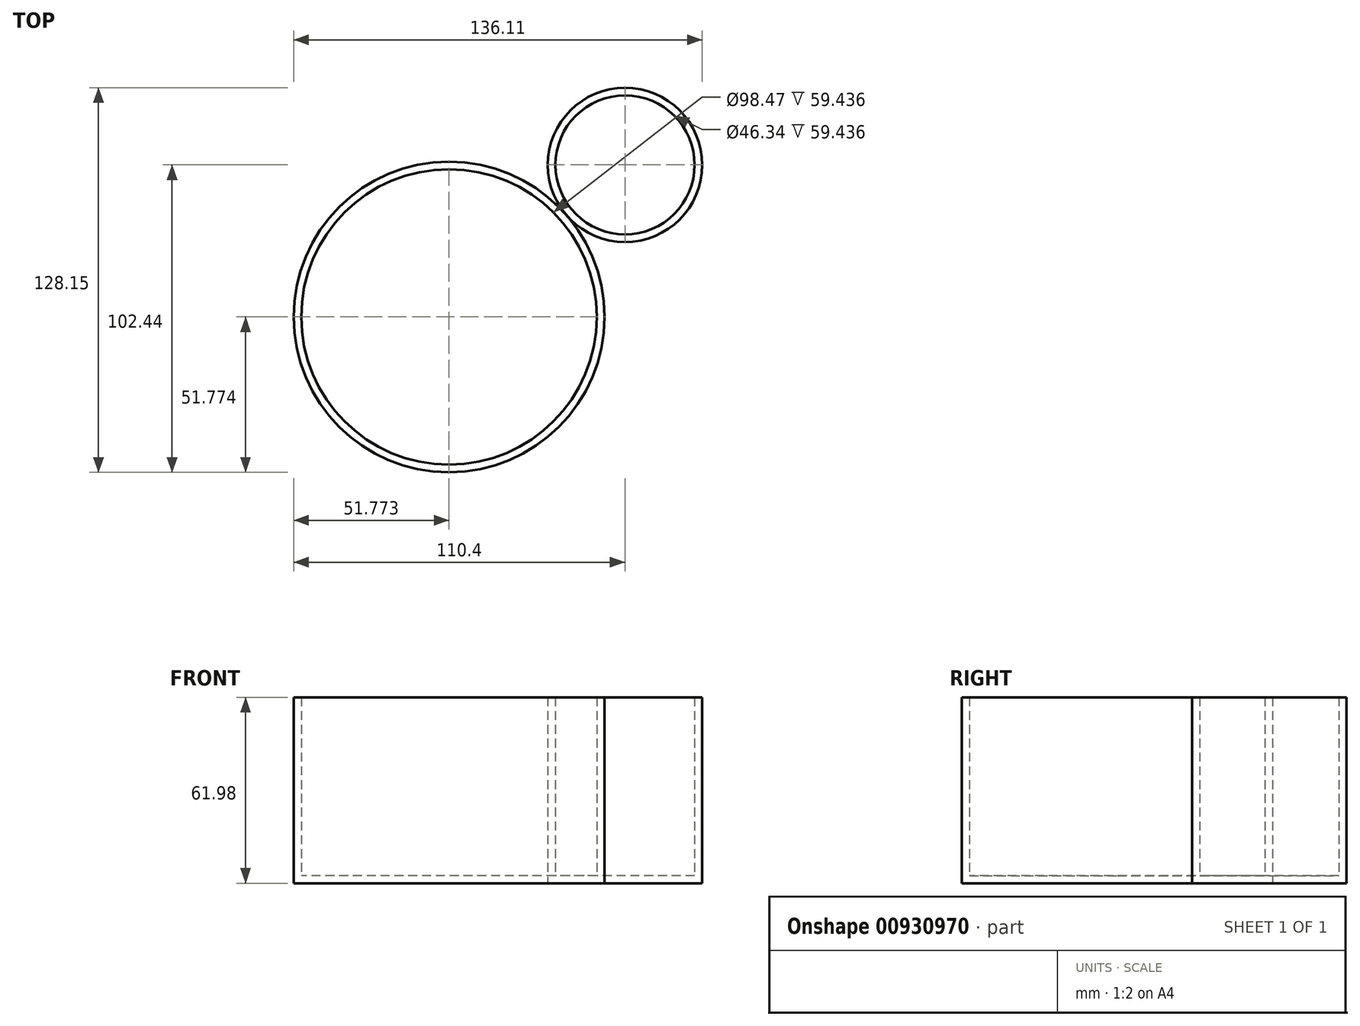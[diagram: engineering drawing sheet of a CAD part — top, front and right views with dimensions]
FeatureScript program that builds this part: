
annotation { "Feature Type Name" : "Feature", "Feature Type Description" : "" }
export const myFeature = defineFeature(function(context is Context, id is Id, definition is map)
    precondition{}
    {
        {
            var Q0;
            Q0=qCreatedBy(makeId("Top.planeOp"),FACE);
            var sketch = newSketch(context, id + "F0", { "sketchPlane" : qUnion([Q0])});
            skCircle(sketch, "E0", {"center": v(-58.63, -50.67) * mm, "radius": 51.77 * mm});
            skCircle(sketch, "E1", {"center": v(0, 0) * mm, "radius": 25.71 * mm});
            skSolve(sketch);
        }
        {
            var Q0;
            Q0 = qSketchRegion(id + "F0", true);
            extrude(context, id + "F1", {"entities" : qUnion([Q0]), "depth" : 61.98 * mm, "offsetDistance" : 25.4 * mm});
        }
        {
            var Q0;
            Q0=makeQuery(id+"F1.opExtrude","CAP_FACE",FACE,{"disambiguationData":[OSD([sQuery(id+"F0.wireOp",EDGE,"E0")])],"isStart":false});
            var Q1;
            Q1=makeQuery(id+"F1.opExtrude","CAP_FACE",FACE,{"disambiguationData":[OSD([sQuery(id+"F0.wireOp",EDGE,"E1")])],"isStart":false});
            shell(context, id + "F2", {"entities" : qUnion([Q0, Q1]), "thickness" : 2.54 * mm});
        }
    });
